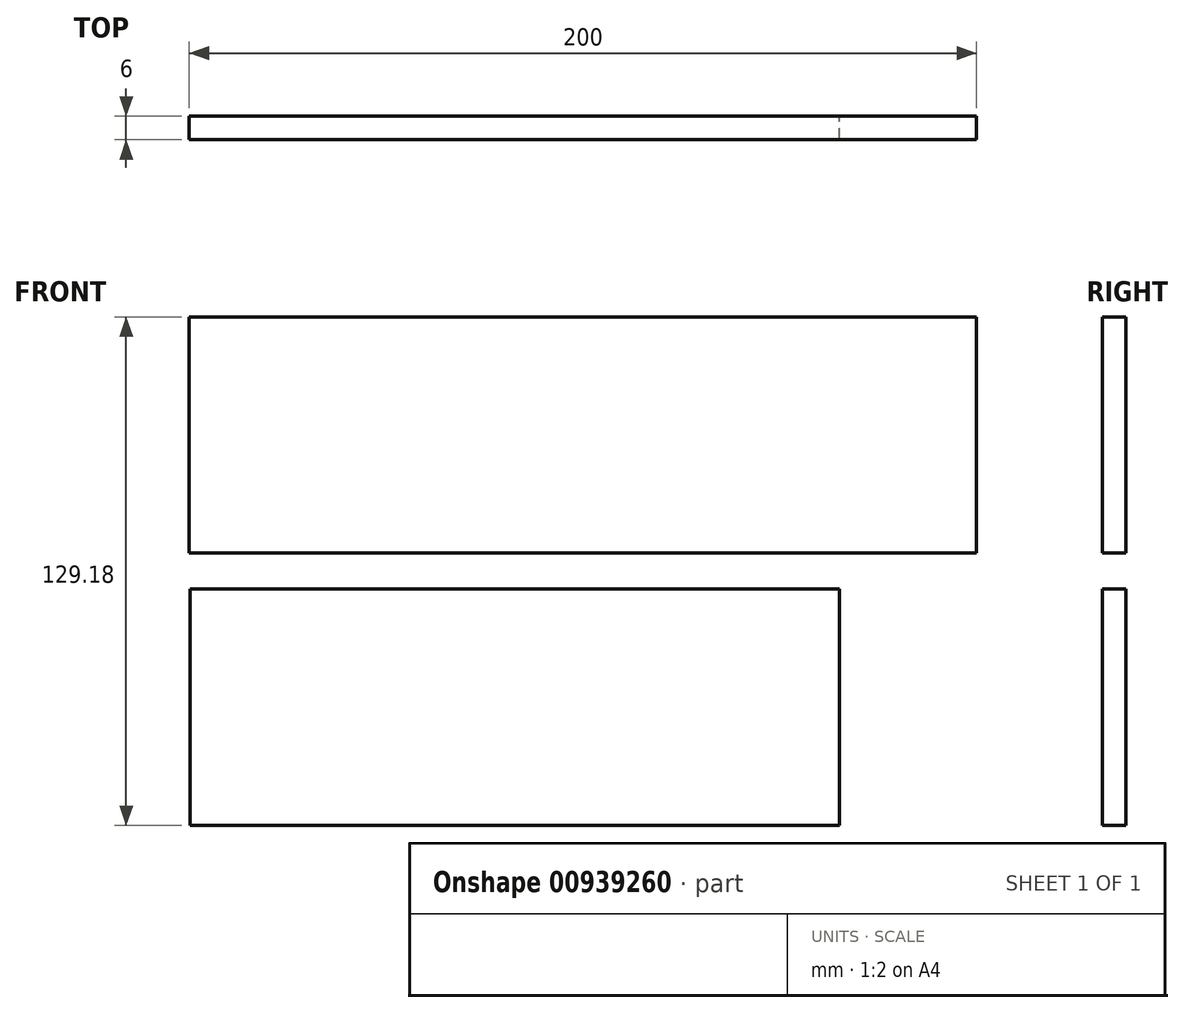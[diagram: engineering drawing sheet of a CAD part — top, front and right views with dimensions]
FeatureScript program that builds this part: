
annotation { "Feature Type Name" : "Feature", "Feature Type Description" : "" }
export const myFeature = defineFeature(function(context is Context, id is Id, definition is map)
    precondition{}
    {
        {
            var Q0;
            Q0=qCreatedBy(makeId("Front.planeOp"),FACE);
            var sketch = newSketch(context, id + "F0", { "sketchPlane" : qUnion([Q0])});
            skLineSegment(sketch, "E0.bottom", {"start": v(-57.02, 28.43) * mm, "end": v(142.98, 28.43) * mm});
            skLineSegment(sketch, "E0.top", {"start": v(-57.02, -31.57) * mm, "end": v(142.98, -31.57) * mm});
            skLineSegment(sketch, "E0.left", {"start": v(-57.02, 28.43) * mm, "end": v(-57.02, -31.57) * mm});
            skLineSegment(sketch, "E0.right", {"start": v(142.98, 28.43) * mm, "end": v(142.98, -31.57) * mm});
            skLineSegment(sketch, "E1.bottom", {"start": v(-56.8, -40.75) * mm, "end": v(108.2, -40.75) * mm});
            skLineSegment(sketch, "E1.top", {"start": v(-56.8, -100.75) * mm, "end": v(108.2, -100.75) * mm});
            skLineSegment(sketch, "E1.left", {"start": v(-56.8, -40.75) * mm, "end": v(-56.8, -100.75) * mm});
            skLineSegment(sketch, "E1.right", {"start": v(108.2, -40.75) * mm, "end": v(108.2, -100.75) * mm});
            skSolve(sketch);
        }
        {
            var Q0;
            Q0=makeQuery(id+"F0.imprint","IMPRINT",FACE,{"disambiguationData":[TD([[makeQuery(id+"F0.imprint","IMPRINT",EDGE,{"derivedFrom":sQuery(id+"F0.wireOp",EDGE,"a6DEvsx4-QgBl-JyJk-JnCB-30eRmNW3zfnj.bottom")}),-1.0]])]});
            var Q1;
            Q1=makeQuery(id+"F0.imprint","IMPRINT",FACE,{"disambiguationData":[TD([[makeQuery(id+"F0.imprint","IMPRINT",EDGE,{"derivedFrom":sQuery(id+"F0.wireOp",EDGE,"E0.bottom")}),-1.0]])]});
            extrude(context, id + "F1", {"entities" : qUnion([Q0, Q1]), "depth" : 6 * mm, "offsetDistance" : 25 * mm});
        }
        {
            var Q0;
            Q0 = qSketchRegion(id + "F0", true);
            extrude(context, id + "F2", {"entities" : qUnion([Q0]), "operationType" : NewBodyOperationType.ADD, "depth" : 6 * mm, "offsetDistance" : 25 * mm});
        }
    });
